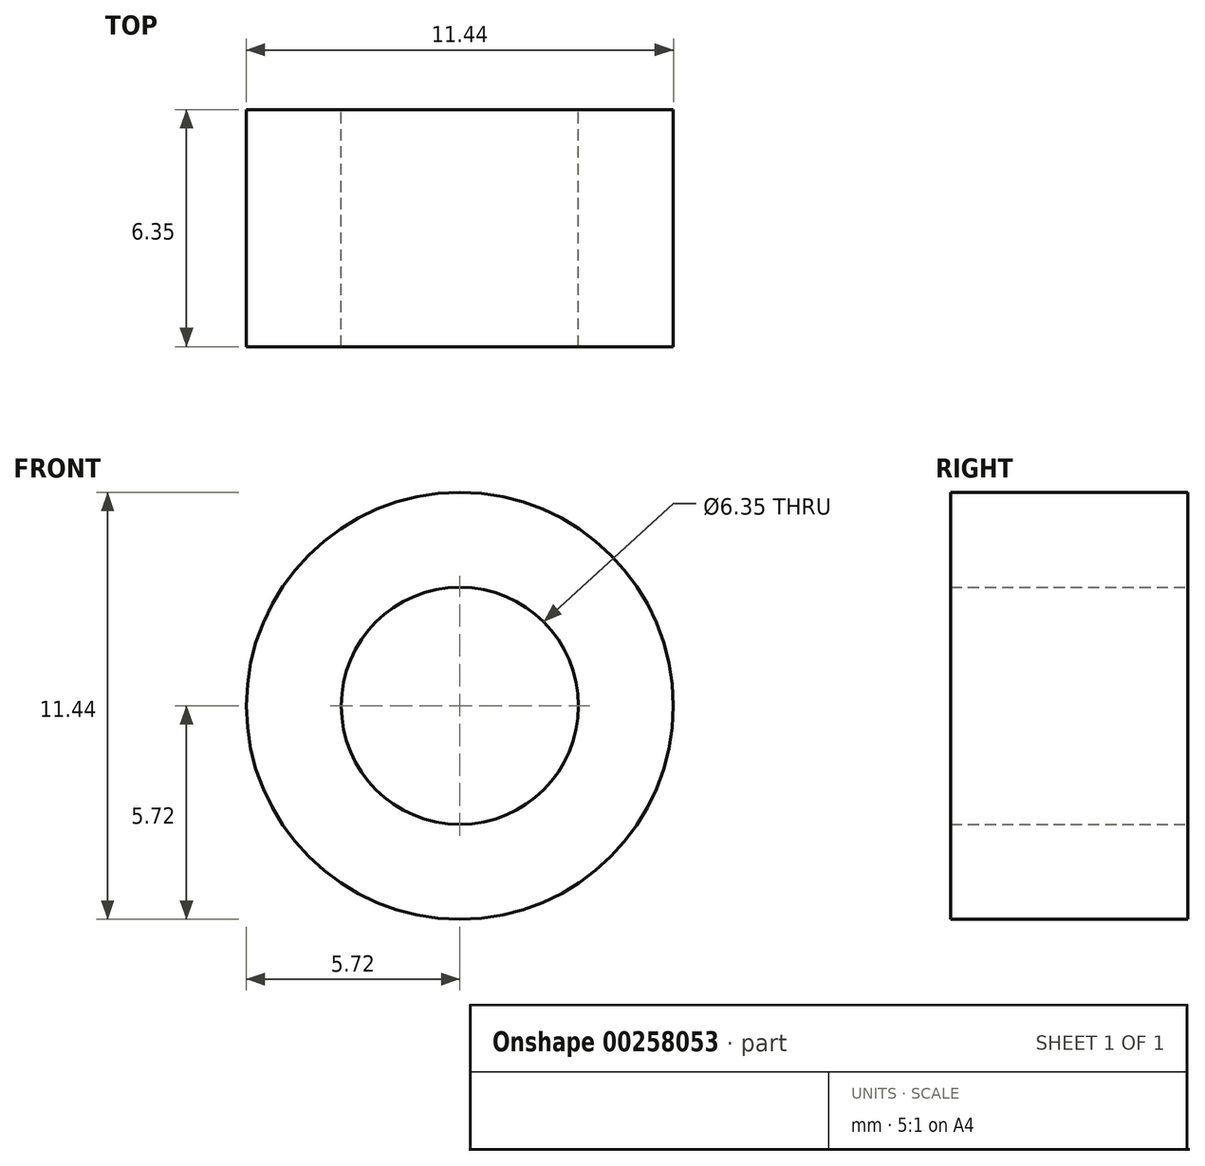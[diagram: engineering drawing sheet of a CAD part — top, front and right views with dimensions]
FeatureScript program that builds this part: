
annotation { "Feature Type Name" : "Feature", "Feature Type Description" : "" }
export const myFeature = defineFeature(function(context is Context, id is Id, definition is map)
    precondition{}
    {
        {
            var Q0;
            Q0=qCreatedBy(makeId("Front.planeOp"),FACE);
            var sketch = newSketch(context, id + "F0", { "sketchPlane" : qUnion([Q0])});
            skCircle(sketch, "E0", {"center": v(0, 0) * mm, "radius": 5.72 * mm});
            skCircle(sketch, "E1", {"center": v(0, 0) * mm, "radius": 3.18 * mm});
            skSolve(sketch);
        }
        {
            var Q0;
            Q0 = qSketchRegion(id + "F0", true);
            extrude(context, id + "F1", {"entities" : qUnion([Q0]), "depth" : 6.35 * mm});
        }
    });
